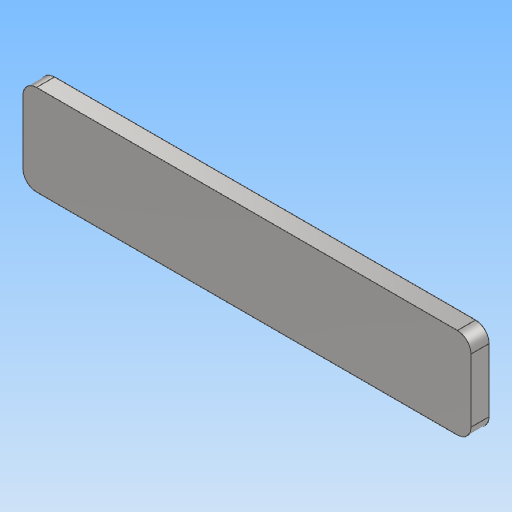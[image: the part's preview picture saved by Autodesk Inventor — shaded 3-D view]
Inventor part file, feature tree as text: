
AUTODESK INVENTOR PART (.ipt)
format: ipt  version: 2020 (Build 240168000, 168)  size: 122,368 bytes
history: native  units: mm
features: other x1, extrude x1
ambient origin geometry x8: Origin, YZ Plane, XZ Plane, XY Plane, X Axis, Y Axis, Z Axis, Center Point
bodies: Body1 (feature_tree)
feature tree (2):
  other  "實體1"
  extrude  "擠出1"  Depth=49.5mm
